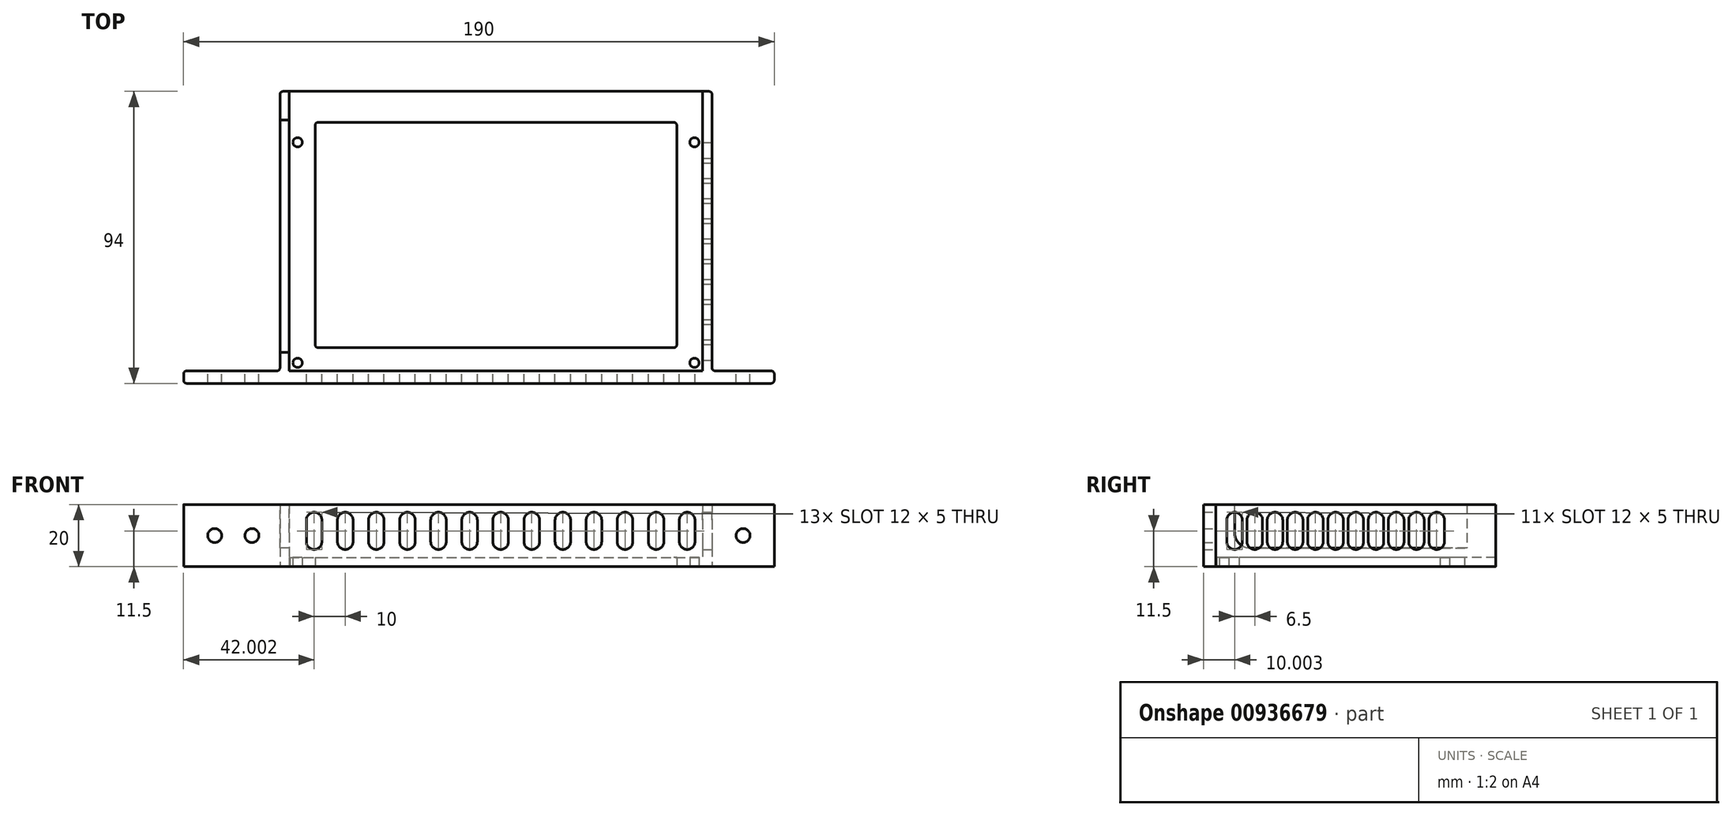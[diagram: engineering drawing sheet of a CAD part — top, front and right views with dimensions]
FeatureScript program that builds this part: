
annotation { "Feature Type Name" : "Feature", "Feature Type Description" : "" }
export const myFeature = defineFeature(function(context is Context, id is Id, definition is map)
    precondition{}
    {
        {
            var Q0;
            Q0=qCreatedBy(makeId("Top.planeOp"),FACE);
            var sketch = newSketch(context, id + "F0", { "sketchPlane" : qUnion([Q0])});
            skLineSegment(sketch, "E0.bottom", {"start": v(-58.92, 42.38) * mm, "end": v(74.08, 42.38) * mm});
            skLineSegment(sketch, "E0.top", {"start": v(-58.72, -47.62) * mm, "end": v(74.08, -47.62) * mm});
            skLineSegment(sketch, "E0.left", {"start": v(-58.92, 42.38) * mm, "end": v(-58.92, -47.62) * mm});
            skLineSegment(sketch, "E0.right", {"start": v(74.08, 42.38) * mm, "end": v(74.08, -47.62) * mm});
            skCircle(sketch, "E1", {"center": v(-56.24, 26) * mm, "radius": 1.5 * mm});
            skCircle(sketch, "E2", {"center": v(-56.24, -45) * mm, "radius": 1.5 * mm});
            skCircle(sketch, "E3", {"center": v(71.4, 26) * mm, "radius": 1.5 * mm});
            skCircle(sketch, "E4", {"center": v(71.4, -45) * mm, "radius": 1.5 * mm});
            skLineSegment(sketch, "E5.bottom", {"start": v(-49.62, 32.38) * mm, "end": v(64.78, 32.38) * mm});
            skLineSegment(sketch, "E5.top", {"start": v(-49.62, -40.12) * mm, "end": v(64.78, -40.12) * mm});
            skLineSegment(sketch, "E5.left", {"start": v(-50.62, 31.38) * mm, "end": v(-50.62, -39.12) * mm});
            skLineSegment(sketch, "E5.right", {"start": v(65.78, 31.38) * mm, "end": v(65.78, -39.12) * mm});
            skLineSegment(sketch, "E6.bottom", {"start": v(-62.92, -47.62) * mm, "end": v(-91.92, -47.62) * mm});
            skLineSegment(sketch, "E6.top", {"start": v(74.08, -51.62) * mm, "end": v(-91.92, -51.62) * mm});
            skLineSegment(sketch, "E6.left", {"start": v(74.08, -47.62) * mm, "end": v(74.08, -51.62) * mm});
            skLineSegment(sketch, "E6.right", {"start": v(-92.92, -48.62) * mm, "end": v(-92.92, -50.62) * mm});
            skLineSegment(sketch, "E7.bottom", {"start": v(74.08, -51.62) * mm, "end": v(77.08, -51.62) * mm});
            skLineSegment(sketch, "E7.top", {"start": v(74.08, 42.38) * mm, "end": v(76.08, 42.38) * mm});
            skLineSegment(sketch, "E7.left", {"start": v(74.08, -51.62) * mm, "end": v(74.08, 42.38) * mm});
            skLineSegment(sketch, "E7.right", {"start": v(77.08, -46.62) * mm, "end": v(77.08, 41.38) * mm});
            skLineSegment(sketch, "E8.bottom", {"start": v(-58.92, 42.38) * mm, "end": v(-60.92, 42.38) * mm});
            skLineSegment(sketch, "E8.top", {"start": v(-58.72, -47.62) * mm, "end": v(-58.92, -47.62) * mm});
            skLineSegment(sketch, "E8.left", {"start": v(-58.92, 42.38) * mm, "end": v(-58.92, -47.42) * mm});
            skLineSegment(sketch, "E8.right", {"start": v(-61.92, 41.38) * mm, "end": v(-61.92, -46.62) * mm});
            skLineSegment(sketch, "E9.bottom", {"start": v(77.08, -51.62) * mm, "end": v(96.08, -51.62) * mm});
            skLineSegment(sketch, "E9.top", {"start": v(78.08, -47.62) * mm, "end": v(96.08, -47.62) * mm});
            skLineSegment(sketch, "E9.right", {"start": v(97.08, -50.62) * mm, "end": v(97.08, -48.62) * mm});
            skPoint(sketch, "E10.visualSharp", {"position": v(-50.62, 32.38) * mm});
            skArc(sketch, "E10.filletArc", {"start": v(-49.62, 32.38) * mm, "mid": v(-50.33, 32.1) * mm, "end": v(-50.62, 31.38) * mm});
            skPoint(sketch, "E11.visualSharp", {"position": v(-50.62, -40.12) * mm});
            skArc(sketch, "E11.filletArc", {"start": v(-50.62, -39.12) * mm, "mid": v(-50.33, -39.82) * mm, "end": v(-49.62, -40.12) * mm});
            skPoint(sketch, "E12.visualSharp", {"position": v(65.78, -40.12) * mm});
            skArc(sketch, "E12.filletArc", {"start": v(64.78, -40.12) * mm, "mid": v(65.49, -39.82) * mm, "end": v(65.78, -39.12) * mm});
            skPoint(sketch, "E13.visualSharp", {"position": v(65.78, 32.38) * mm});
            skArc(sketch, "E13.filletArc", {"start": v(65.78, 31.38) * mm, "mid": v(65.49, 32.1) * mm, "end": v(64.78, 32.38) * mm});
            skPoint(sketch, "E14.visualSharp", {"position": v(-61.92, 42.38) * mm});
            skArc(sketch, "E14.filletArc", {"start": v(-60.92, 42.38) * mm, "mid": v(-61.63, 42.1) * mm, "end": v(-61.92, 41.38) * mm});
            skArc(sketch, "E15.filletArc", {"start": v(-62.92, -47.62) * mm, "mid": v(-62.21, -47.32) * mm, "end": v(-61.92, -46.62) * mm});
            skPoint(sketch, "E16.visualSharp", {"position": v(-92.92, -51.62) * mm});
            skArc(sketch, "E16.filletArc", {"start": v(-92.92, -50.62) * mm, "mid": v(-92.63, -51.32) * mm, "end": v(-91.92, -51.62) * mm});
            skPoint(sketch, "E17.visualSharp", {"position": v(-92.92, -47.62) * mm});
            skArc(sketch, "E17.filletArc", {"start": v(-91.92, -47.62) * mm, "mid": v(-92.63, -47.9) * mm, "end": v(-92.92, -48.62) * mm});
            skPoint(sketch, "E18.visualSharp", {"position": v(97.08, -51.62) * mm});
            skArc(sketch, "E18.filletArc", {"start": v(96.08, -51.62) * mm, "mid": v(96.79, -51.32) * mm, "end": v(97.08, -50.62) * mm});
            skPoint(sketch, "E19.visualSharp", {"position": v(97.08, -47.62) * mm});
            skArc(sketch, "E19.filletArc", {"start": v(97.08, -48.62) * mm, "mid": v(96.79, -47.9) * mm, "end": v(96.08, -47.62) * mm});
            skPoint(sketch, "E20.visualSharp", {"position": v(77.08, 42.38) * mm});
            skArc(sketch, "E20.filletArc", {"start": v(77.08, 41.38) * mm, "mid": v(76.79, 42.1) * mm, "end": v(76.08, 42.38) * mm});
            skPoint(sketch, "E21.visualSharp", {"position": v(-58.92, -47.62) * mm});
            skArc(sketch, "E21.filletArc", {"start": v(-58.92, -47.42) * mm, "mid": v(-58.86, -47.56) * mm, "end": v(-58.72, -47.62) * mm});
            skArc(sketch, "E22.filletArc", {"start": v(77.08, -46.62) * mm, "mid": v(77.37, -47.32) * mm, "end": v(78.08, -47.62) * mm});
            skSolve(sketch);
        }
        {
            var Q0;
            {var subQ0=sQuery(id+"F0.wireOp",EDGE,"E0.bottom");Q0=makeQuery(id+"F0.imprint","IMPRINT",FACE,{"disambiguationData":[TD([[makeQuery(id+"F0.imprint","IMPRINT",EDGE,{"derivedFrom":subQ0}),-1.0]])]});}
            extrude(context, id + "F1", {"entities" : qUnion([Q0]), "depth" : 3 * mm, "offsetDistance" : 25 * mm});
        }
        {
            var Q0;
            {var subQ0=sQuery(id+"F0.wireOp",EDGE,"E0.top");Q0=makeQuery(id+"F0.imprint","IMPRINT",FACE,{"disambiguationData":[TD([[makeQuery(id+"F0.imprint","IMPRINT",EDGE,{"derivedFrom":subQ0}),-1.0]])]});}
            var Q1;
            {var subQ3=sQuery(id+"F0.wireOp",EDGE,"E7.bottom");Q1=makeQuery(id+"F0.imprint","IMPRINT",FACE,{"disambiguationData":[TD([[makeQuery(id+"F0.imprint","IMPRINT",EDGE,{"derivedFrom":subQ3}),1.0]])]});}
            var Q2;
            Q2=makeQuery(id+"F0.imprint","IMPRINT",FACE,{"disambiguationData":[TD([[makeQuery(id+"F0.imprint","IMPRINT",EDGE,{"derivedFrom":sQuery(id+"F0.wireOp",EDGE,"E8.bottom")}),1.0]])]});
            var Q3;
            Q3=makeQuery(id+"F0.imprint","IMPRINT",FACE,{"disambiguationData":[TD([[makeQuery(id+"F0.imprint","IMPRINT",EDGE,{"derivedFrom":sQuery(id+"F0.wireOp",EDGE,"E9.bottom")}),1.0]])]});
            extrude(context, id + "F2", {"entities" : qUnion([Q0, Q1, Q2, Q3]), "operationType" : NewBodyOperationType.ADD, "depth" : 20 * mm, "offsetDistance" : 25 * mm});
        }
        {
            var Q0;
            Q0=makeQuery(id+"F2.opExtrude","SWEPT_FACE",FACE,{"disambiguationData":[OSD([sQuery(id+"F0.wireOp",EDGE,"E7.right")])]});
            var sketch = newSketch(context, id + "F3", { "sketchPlane" : qUnion([Q0])});
            skLineSegment(sketch, "E23", {"start": v(-41.62, 15) * mm, "end": v(-41.62, 8) * mm, "construction": true});
            skArc(sketch, "E24", {"start": v(-39.12, 15) * mm, "mid": v(-41.62, 17.5) * mm, "end": v(-44.12, 15) * mm});
            skArc(sketch, "E25", {"start": v(-44.12, 8) * mm, "mid": v(-41.62, 5.5) * mm, "end": v(-39.12, 8) * mm});
            skLineSegment(sketch, "E26", {"start": v(-44.12, 15) * mm, "end": v(-44.12, 8) * mm});
            skLineSegment(sketch, "E27", {"start": v(-39.12, 15) * mm, "end": v(-39.12, 8) * mm});
            skLineSegment(sketch, "E28", {"start": v(-41.62, 8) * mm, "end": v(33.9, 8) * mm, "construction": true});
            skLineSegment(sketch, "E29.1.0.0", {"start": v(-32.62, 15) * mm, "end": v(-32.62, 8) * mm});
            skLineSegment(sketch, "E29.1.0.1", {"start": v(-35.12, 15) * mm, "end": v(-35.12, 8) * mm, "construction": true});
            skArc(sketch, "E29.1.0.2", {"start": v(-32.62, 15) * mm, "mid": v(-35.12, 17.5) * mm, "end": v(-37.62, 15) * mm});
            skArc(sketch, "E29.1.0.3", {"start": v(-37.62, 8) * mm, "mid": v(-35.12, 5.5) * mm, "end": v(-32.62, 8) * mm});
            skLineSegment(sketch, "E29.1.0.4", {"start": v(-37.62, 15) * mm, "end": v(-37.62, 8) * mm});
            skLineSegment(sketch, "E29.2.0.0", {"start": v(-26.12, 15) * mm, "end": v(-26.12, 8) * mm});
            skLineSegment(sketch, "E29.2.0.1", {"start": v(-28.62, 15) * mm, "end": v(-28.62, 8) * mm, "construction": true});
            skArc(sketch, "E29.2.0.2", {"start": v(-26.12, 15) * mm, "mid": v(-28.62, 17.5) * mm, "end": v(-31.12, 15) * mm});
            skArc(sketch, "E29.2.0.3", {"start": v(-31.12, 8) * mm, "mid": v(-28.62, 5.5) * mm, "end": v(-26.12, 8) * mm});
            skLineSegment(sketch, "E29.2.0.4", {"start": v(-31.12, 15) * mm, "end": v(-31.12, 8) * mm});
            skLineSegment(sketch, "E29.3.0.0", {"start": v(-19.62, 15) * mm, "end": v(-19.62, 8) * mm});
            skLineSegment(sketch, "E29.3.0.1", {"start": v(-22.12, 15) * mm, "end": v(-22.12, 8) * mm, "construction": true});
            skArc(sketch, "E29.3.0.2", {"start": v(-19.62, 15) * mm, "mid": v(-22.12, 17.5) * mm, "end": v(-24.62, 15) * mm});
            skArc(sketch, "E29.3.0.3", {"start": v(-24.62, 8) * mm, "mid": v(-22.12, 5.5) * mm, "end": v(-19.62, 8) * mm});
            skLineSegment(sketch, "E29.3.0.4", {"start": v(-24.62, 15) * mm, "end": v(-24.62, 8) * mm});
            skLineSegment(sketch, "E29.4.0.0", {"start": v(-13.12, 15) * mm, "end": v(-13.12, 8) * mm});
            skLineSegment(sketch, "E29.4.0.1", {"start": v(-15.62, 15) * mm, "end": v(-15.62, 8) * mm, "construction": true});
            skArc(sketch, "E29.4.0.2", {"start": v(-13.12, 15) * mm, "mid": v(-15.62, 17.5) * mm, "end": v(-18.12, 15) * mm});
            skArc(sketch, "E29.4.0.3", {"start": v(-18.12, 8) * mm, "mid": v(-15.62, 5.5) * mm, "end": v(-13.12, 8) * mm});
            skLineSegment(sketch, "E29.4.0.4", {"start": v(-18.12, 15) * mm, "end": v(-18.12, 8) * mm});
            skLineSegment(sketch, "E29.5.0.0", {"start": v(-6.62, 15) * mm, "end": v(-6.62, 8) * mm});
            skLineSegment(sketch, "E29.5.0.1", {"start": v(-9.12, 15) * mm, "end": v(-9.12, 8) * mm, "construction": true});
            skArc(sketch, "E29.5.0.2", {"start": v(-6.62, 15) * mm, "mid": v(-9.12, 17.5) * mm, "end": v(-11.62, 15) * mm});
            skArc(sketch, "E29.5.0.3", {"start": v(-11.62, 8) * mm, "mid": v(-9.12, 5.5) * mm, "end": v(-6.62, 8) * mm});
            skLineSegment(sketch, "E29.5.0.4", {"start": v(-11.62, 15) * mm, "end": v(-11.62, 8) * mm});
            skLineSegment(sketch, "E29.6.0.0", {"start": v(-0.12, 15) * mm, "end": v(-0.12, 8) * mm});
            skLineSegment(sketch, "E29.6.0.1", {"start": v(-2.62, 15) * mm, "end": v(-2.62, 8) * mm, "construction": true});
            skArc(sketch, "E29.6.0.2", {"start": v(-0.12, 15) * mm, "mid": v(-2.62, 17.5) * mm, "end": v(-5.12, 15) * mm});
            skArc(sketch, "E29.6.0.3", {"start": v(-5.12, 8) * mm, "mid": v(-2.62, 5.5) * mm, "end": v(-0.12, 8) * mm});
            skLineSegment(sketch, "E29.6.0.4", {"start": v(-5.12, 15) * mm, "end": v(-5.12, 8) * mm});
            skLineSegment(sketch, "E29.7.0.0", {"start": v(6.38, 15) * mm, "end": v(6.38, 8) * mm});
            skLineSegment(sketch, "E29.7.0.1", {"start": v(3.88, 15) * mm, "end": v(3.88, 8) * mm, "construction": true});
            skArc(sketch, "E29.7.0.2", {"start": v(6.38, 15) * mm, "mid": v(3.88, 17.5) * mm, "end": v(1.38, 15) * mm});
            skArc(sketch, "E29.7.0.3", {"start": v(1.38, 8) * mm, "mid": v(3.88, 5.5) * mm, "end": v(6.38, 8) * mm});
            skLineSegment(sketch, "E29.7.0.4", {"start": v(1.38, 15) * mm, "end": v(1.38, 8) * mm});
            skLineSegment(sketch, "E29.8.0.0", {"start": v(12.88, 15) * mm, "end": v(12.88, 8) * mm});
            skLineSegment(sketch, "E29.8.0.1", {"start": v(10.38, 15) * mm, "end": v(10.38, 8) * mm, "construction": true});
            skArc(sketch, "E29.8.0.2", {"start": v(12.88, 15) * mm, "mid": v(10.38, 17.5) * mm, "end": v(7.88, 15) * mm});
            skArc(sketch, "E29.8.0.3", {"start": v(7.88, 8) * mm, "mid": v(10.38, 5.5) * mm, "end": v(12.88, 8) * mm});
            skLineSegment(sketch, "E29.8.0.4", {"start": v(7.88, 15) * mm, "end": v(7.88, 8) * mm});
            skLineSegment(sketch, "E29.9.0.0", {"start": v(19.38, 15) * mm, "end": v(19.38, 8) * mm});
            skLineSegment(sketch, "E29.9.0.1", {"start": v(16.88, 15) * mm, "end": v(16.88, 8) * mm, "construction": true});
            skArc(sketch, "E29.9.0.2", {"start": v(19.38, 15) * mm, "mid": v(16.88, 17.5) * mm, "end": v(14.38, 15) * mm});
            skArc(sketch, "E29.9.0.3", {"start": v(14.38, 8) * mm, "mid": v(16.88, 5.5) * mm, "end": v(19.38, 8) * mm});
            skLineSegment(sketch, "E29.9.0.4", {"start": v(14.38, 15) * mm, "end": v(14.38, 8) * mm});
            skLineSegment(sketch, "E29.10.0.0", {"start": v(25.88, 15) * mm, "end": v(25.88, 8) * mm});
            skLineSegment(sketch, "E29.10.0.1", {"start": v(23.38, 15) * mm, "end": v(23.38, 8) * mm, "construction": true});
            skArc(sketch, "E29.10.0.2", {"start": v(25.88, 15) * mm, "mid": v(23.38, 17.5) * mm, "end": v(20.88, 15) * mm});
            skArc(sketch, "E29.10.0.3", {"start": v(20.88, 8) * mm, "mid": v(23.38, 5.5) * mm, "end": v(25.88, 8) * mm});
            skLineSegment(sketch, "E29.10.0.4", {"start": v(20.88, 15) * mm, "end": v(20.88, 8) * mm});
            skLineSegment(sketch, "E29.direction1", {"start": v(-44.12, 8) * mm, "end": v(-37.62, 8) * mm, "construction": true});
            skSolve(sketch);
        }
        {
            var Q0;
            Q0 = qSketchRegion(id + "F3", true);
            extrude(context, id + "F4", {"entities" : qUnion([Q0]), "operationType" : NewBodyOperationType.REMOVE, "oppositeDirection" : true, "depth" : 10 * mm, "offsetDistance" : 25 * mm});
        }
        {
            var Q0;
            Q0=makeQuery(id+"F2.opExtrude","SWEPT_FACE",FACE,{"disambiguationData":[OSD([sQuery(id+"F0.wireOp",EDGE,"E8.right")])]});
            var sketch = newSketch(context, id + "F5", { "sketchPlane" : qUnion([Q0])});
            skLineSegment(sketch, "E30", {"start": v(41.62, 26.3) * mm, "end": v(41.62, 11) * mm});
            skLineSegment(sketch, "E31", {"start": v(-178.12, 6) * mm, "end": v(36.62, 6) * mm});
            skArc(sketch, "E32.filletArc", {"start": v(36.62, 6) * mm, "mid": v(40.15, 7.46) * mm, "end": v(41.62, 11) * mm});
            skLineSegment(sketch, "E33", {"start": v(-33.12, 6) * mm, "end": v(-33.12, 26.3) * mm});
            skLineSegment(sketch, "E34", {"start": v(-33.12, 26.3) * mm, "end": v(41.62, 26.3) * mm});
            skPoint(sketch, "E35.orphan", {"position": v(41.62, 20) * mm});
            skSolve(sketch);
        }
        {
            var Q0;
            {var subQ1=sQuery(id+"F5.wireOp",EDGE,"E33");Q0=makeQuery(id+"F5.imprint","IMPRINT",FACE,{"disambiguationData":[TD([[makeQuery(id+"F5.imprint","IMPRINT",EDGE,{"derivedFrom":subQ1}),-1.0]])]});}
            var Q1;
            {var subQ6=sQuery(id+"F5.wireOp",EDGE,"E32.filletArc");Q1=makeQuery(id+"F5.imprint","IMPRINT",FACE,{"disambiguationData":[TD([[makeQuery(id+"F5.imprint","IMPRINT",EDGE,{"derivedFrom":subQ6}),1.0]])]});}
            extrude(context, id + "F6", {"entities" : qUnion([Q0, Q1]), "operationType" : NewBodyOperationType.REMOVE, "oppositeDirection" : true, "depth" : 15 * mm, "offsetDistance" : 25 * mm});
        }
        {
            var Q0;
            Q0=makeQuery(id+"F2.opExtrude","SWEPT_FACE",FACE,{"disambiguationData":[OSD([sQuery(id+"F0.wireOp",EDGE,"E6.bottom")])]});
            var sketch = newSketch(context, id + "F7", { "sketchPlane" : qUnion([Q0])});
            skPoint(sketch, "E36.0", {"position": v(-96.08, 10) * mm});
            skPoint(sketch, "E37.0", {"position": v(91.92, 10) * mm});
            skLineSegment(sketch, "E38", {"start": v(-96.08, 10) * mm, "end": v(91.92, 10) * mm, "construction": true});
            skCircle(sketch, "E39", {"center": v(-87.08, 10) * mm, "radius": 2.25 * mm});
            skCircle(sketch, "E40", {"center": v(70.92, 10) * mm, "radius": 2.25 * mm});
            skCircle(sketch, "E41", {"center": v(82.92, 10) * mm, "radius": 2.25 * mm});
            skSolve(sketch);
        }
        {
            var Q0;
            Q0=makeQuery(id+"F7.imprint","IMPRINT",FACE,{"disambiguationData":[TD([[makeQuery(id+"F7.imprint","IMPRINT",EDGE,{"derivedFrom":sQuery(id+"F7.wireOp",EDGE,"E39")}),1.0]])]});
            var Q1;
            Q1=makeQuery(id+"F7.imprint","IMPRINT",FACE,{"disambiguationData":[TD([[makeQuery(id+"F7.imprint","IMPRINT",EDGE,{"derivedFrom":sQuery(id+"F7.wireOp",EDGE,"E40")}),1.0]])]});
            var Q2;
            Q2=makeQuery(id+"F7.imprint","IMPRINT",FACE,{"disambiguationData":[TD([[makeQuery(id+"F7.imprint","IMPRINT",EDGE,{"derivedFrom":sQuery(id+"F7.wireOp",EDGE,"E41")}),1.0]])]});
            extrude(context, id + "F8", {"entities" : qUnion([Q0, Q1, Q2]), "operationType" : NewBodyOperationType.REMOVE, "oppositeDirection" : true, "depth" : 25 * mm, "offsetDistance" : 25 * mm});
        }
        {
            var Q0;
            Q0=makeQuery(id+"F2.opExtrude","SWEPT_FACE",FACE,{"disambiguationData":[OSD([sQuery(id+"F0.wireOp",EDGE,"E0.top"),sQuery(id+"F0.wireOp",EDGE,"E8.top")])]});
            var sketch = newSketch(context, id + "F9", { "sketchPlane" : qUnion([Q0])});
            skLineSegment(sketch, "E42", {"start": v(-74.08, 11.5) * mm, "end": v(58.92, 12.3) * mm, "construction": true});
            skArc(sketch, "E43", {"start": v(-66.58, 15) * mm, "mid": v(-69.08, 17.5) * mm, "end": v(-71.58, 15) * mm});
            skArc(sketch, "E44", {"start": v(-71.58, 8) * mm, "mid": v(-69.08, 5.5) * mm, "end": v(-66.58, 8) * mm});
            skLineSegment(sketch, "E45", {"start": v(-71.58, 15) * mm, "end": v(-71.58, 8) * mm});
            skLineSegment(sketch, "E46", {"start": v(-66.58, 15) * mm, "end": v(-66.58, 8) * mm});
            skArc(sketch, "E47.1.0.0", {"start": v(-61.58, 8) * mm, "mid": v(-59.08, 5.5) * mm, "end": v(-56.58, 8) * mm});
            skLineSegment(sketch, "E47.1.0.1", {"start": v(-56.58, 15) * mm, "end": v(-56.58, 8) * mm});
            skLineSegment(sketch, "E47.1.0.2", {"start": v(-61.58, 15) * mm, "end": v(-61.58, 8) * mm});
            skArc(sketch, "E47.1.0.3", {"start": v(-56.58, 15) * mm, "mid": v(-59.08, 17.5) * mm, "end": v(-61.58, 15) * mm});
            skArc(sketch, "E47.2.0.0", {"start": v(-51.58, 8) * mm, "mid": v(-49.08, 5.5) * mm, "end": v(-46.58, 8) * mm});
            skLineSegment(sketch, "E47.2.0.1", {"start": v(-46.58, 15) * mm, "end": v(-46.58, 8) * mm});
            skLineSegment(sketch, "E47.2.0.2", {"start": v(-51.58, 15) * mm, "end": v(-51.58, 8) * mm});
            skArc(sketch, "E47.2.0.3", {"start": v(-46.58, 15) * mm, "mid": v(-49.08, 17.5) * mm, "end": v(-51.58, 15) * mm});
            skArc(sketch, "E47.3.0.0", {"start": v(-41.58, 8) * mm, "mid": v(-39.08, 5.5) * mm, "end": v(-36.58, 8) * mm});
            skLineSegment(sketch, "E47.3.0.1", {"start": v(-36.58, 15) * mm, "end": v(-36.58, 8) * mm});
            skLineSegment(sketch, "E47.3.0.2", {"start": v(-41.58, 15) * mm, "end": v(-41.58, 8) * mm});
            skArc(sketch, "E47.3.0.3", {"start": v(-36.58, 15) * mm, "mid": v(-39.08, 17.5) * mm, "end": v(-41.58, 15) * mm});
            skArc(sketch, "E47.4.0.0", {"start": v(-31.58, 8) * mm, "mid": v(-29.08, 5.5) * mm, "end": v(-26.58, 8) * mm});
            skLineSegment(sketch, "E47.4.0.1", {"start": v(-26.58, 15) * mm, "end": v(-26.58, 8) * mm});
            skLineSegment(sketch, "E47.4.0.2", {"start": v(-31.58, 15) * mm, "end": v(-31.58, 8) * mm});
            skArc(sketch, "E47.4.0.3", {"start": v(-26.58, 15) * mm, "mid": v(-29.08, 17.5) * mm, "end": v(-31.58, 15) * mm});
            skArc(sketch, "E47.5.0.0", {"start": v(-21.58, 8) * mm, "mid": v(-19.08, 5.5) * mm, "end": v(-16.58, 8) * mm});
            skLineSegment(sketch, "E47.5.0.1", {"start": v(-16.58, 15) * mm, "end": v(-16.58, 8) * mm});
            skLineSegment(sketch, "E47.5.0.2", {"start": v(-21.58, 15) * mm, "end": v(-21.58, 8) * mm});
            skArc(sketch, "E47.5.0.3", {"start": v(-16.58, 15) * mm, "mid": v(-19.08, 17.5) * mm, "end": v(-21.58, 15) * mm});
            skArc(sketch, "E47.6.0.0", {"start": v(-11.58, 8) * mm, "mid": v(-9.08, 5.5) * mm, "end": v(-6.58, 8) * mm});
            skLineSegment(sketch, "E47.6.0.1", {"start": v(-6.58, 15) * mm, "end": v(-6.58, 8) * mm});
            skLineSegment(sketch, "E47.6.0.2", {"start": v(-11.58, 15) * mm, "end": v(-11.58, 8) * mm});
            skArc(sketch, "E47.6.0.3", {"start": v(-6.58, 15) * mm, "mid": v(-9.08, 17.5) * mm, "end": v(-11.58, 15) * mm});
            skArc(sketch, "E47.7.0.0", {"start": v(-1.58, 8) * mm, "mid": v(0.92, 5.5) * mm, "end": v(3.42, 8) * mm});
            skLineSegment(sketch, "E47.7.0.1", {"start": v(3.42, 15) * mm, "end": v(3.42, 8) * mm});
            skLineSegment(sketch, "E47.7.0.2", {"start": v(-1.58, 15) * mm, "end": v(-1.58, 8) * mm});
            skArc(sketch, "E47.7.0.3", {"start": v(3.42, 15) * mm, "mid": v(0.92, 17.5) * mm, "end": v(-1.58, 15) * mm});
            skArc(sketch, "E47.8.0.0", {"start": v(8.42, 8) * mm, "mid": v(10.92, 5.5) * mm, "end": v(13.42, 8) * mm});
            skLineSegment(sketch, "E47.8.0.1", {"start": v(13.42, 15) * mm, "end": v(13.42, 8) * mm});
            skLineSegment(sketch, "E47.8.0.2", {"start": v(8.42, 15) * mm, "end": v(8.42, 8) * mm});
            skArc(sketch, "E47.8.0.3", {"start": v(13.42, 15) * mm, "mid": v(10.92, 17.5) * mm, "end": v(8.42, 15) * mm});
            skArc(sketch, "E47.9.0.0", {"start": v(18.42, 8) * mm, "mid": v(20.92, 5.5) * mm, "end": v(23.42, 8) * mm});
            skLineSegment(sketch, "E47.9.0.1", {"start": v(23.42, 15) * mm, "end": v(23.42, 8) * mm});
            skLineSegment(sketch, "E47.9.0.2", {"start": v(18.42, 15) * mm, "end": v(18.42, 8) * mm});
            skArc(sketch, "E47.9.0.3", {"start": v(23.42, 15) * mm, "mid": v(20.92, 17.5) * mm, "end": v(18.42, 15) * mm});
            skArc(sketch, "E47.10.0.0", {"start": v(28.42, 8) * mm, "mid": v(30.92, 5.5) * mm, "end": v(33.42, 8) * mm});
            skLineSegment(sketch, "E47.10.0.1", {"start": v(33.42, 15) * mm, "end": v(33.42, 8) * mm});
            skLineSegment(sketch, "E47.10.0.2", {"start": v(28.42, 15) * mm, "end": v(28.42, 8) * mm});
            skArc(sketch, "E47.10.0.3", {"start": v(33.42, 15) * mm, "mid": v(30.92, 17.5) * mm, "end": v(28.42, 15) * mm});
            skArc(sketch, "E47.11.0.0", {"start": v(38.42, 8) * mm, "mid": v(40.92, 5.5) * mm, "end": v(43.42, 8) * mm});
            skLineSegment(sketch, "E47.11.0.1", {"start": v(43.42, 15) * mm, "end": v(43.42, 8) * mm});
            skLineSegment(sketch, "E47.11.0.2", {"start": v(38.42, 15) * mm, "end": v(38.42, 8) * mm});
            skArc(sketch, "E47.11.0.3", {"start": v(43.42, 15) * mm, "mid": v(40.92, 17.5) * mm, "end": v(38.42, 15) * mm});
            skArc(sketch, "E47.12.0.0", {"start": v(48.42, 8) * mm, "mid": v(50.92, 5.5) * mm, "end": v(53.42, 8) * mm});
            skLineSegment(sketch, "E47.12.0.1", {"start": v(53.42, 15) * mm, "end": v(53.42, 8) * mm});
            skLineSegment(sketch, "E47.12.0.2", {"start": v(48.42, 15) * mm, "end": v(48.42, 8) * mm});
            skArc(sketch, "E47.12.0.3", {"start": v(53.42, 15) * mm, "mid": v(50.92, 17.5) * mm, "end": v(48.42, 15) * mm});
            skLineSegment(sketch, "E47.direction1", {"start": v(-71.58, 8) * mm, "end": v(-61.58, 8) * mm, "construction": true});
            skSolve(sketch);
        }
        {
            var Q0;
            Q0 = qSketchRegion(id + "F9", true);
            extrude(context, id + "F10", {"entities" : qUnion([Q0]), "operationType" : NewBodyOperationType.REMOVE, "oppositeDirection" : true, "depth" : 25 * mm, "offsetDistance" : 25 * mm});
        }
    });
